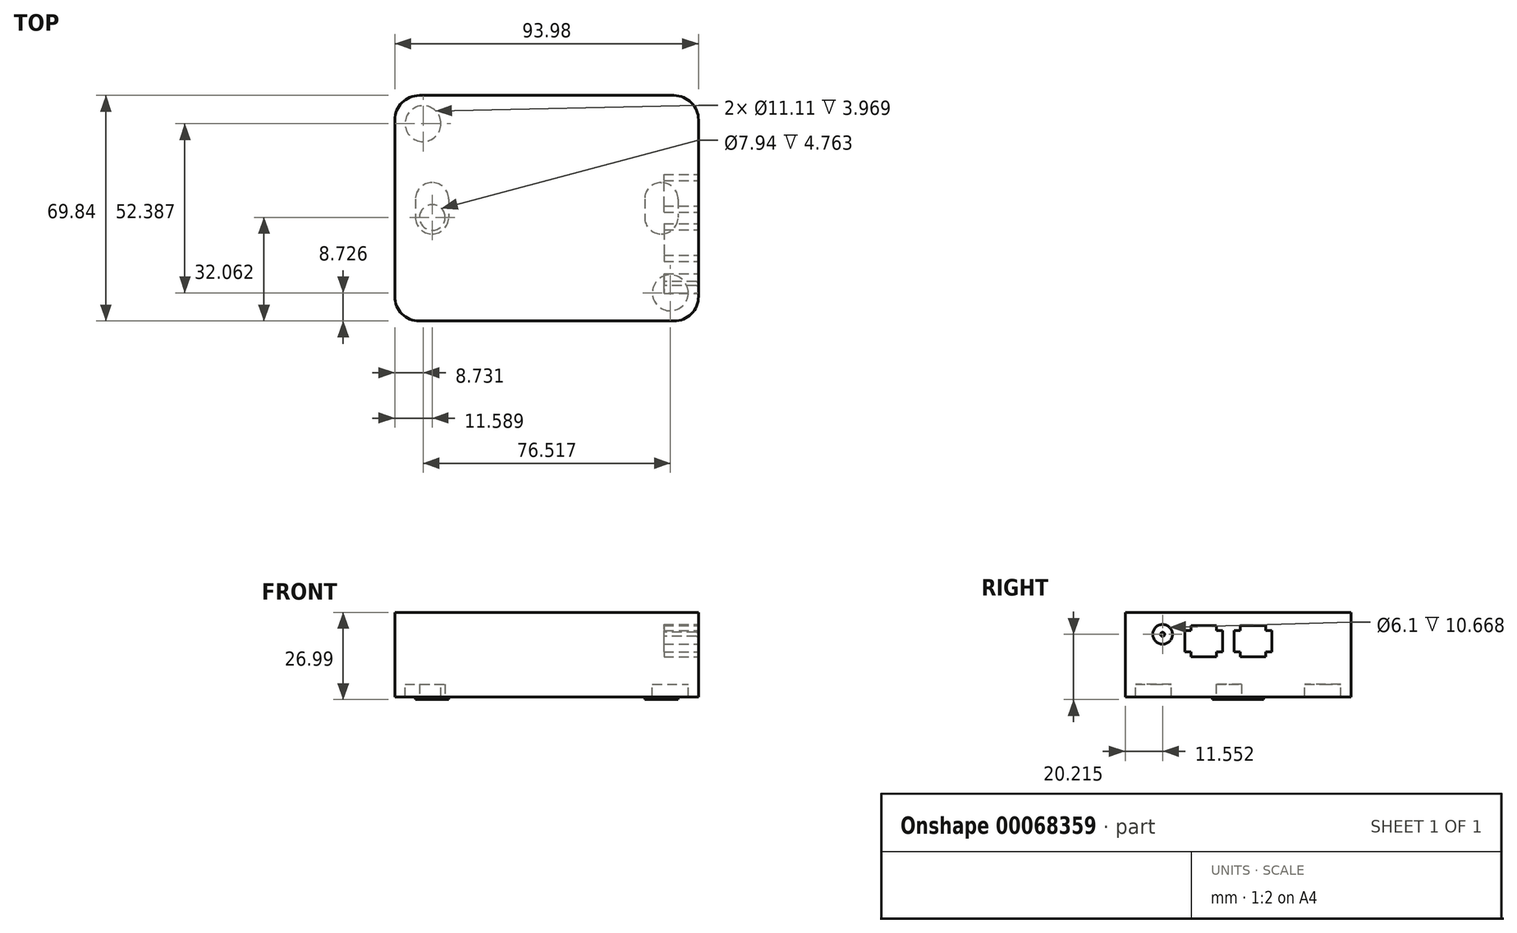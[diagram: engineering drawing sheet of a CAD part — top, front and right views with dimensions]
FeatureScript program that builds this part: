
annotation { "Feature Type Name" : "Feature", "Feature Type Description" : "" }
export const myFeature = defineFeature(function(context is Context, id is Id, definition is map)
    precondition{}
    {
        {
            var Q0;
            Q0=qCreatedBy(makeId("Top.planeOp"),FACE);
            var sketch = newSketch(context, id + "F0", { "sketchPlane" : qUnion([Q0])});
            skLineSegment(sketch, "E0.rect.bottom", {"start": v(47, -34.93) * mm, "end": v(-47, -34.93) * mm});
            skLineSegment(sketch, "E0.rect.top", {"start": v(47, 34.93) * mm, "end": v(-47, 34.92) * mm});
            skLineSegment(sketch, "E0.rect.left", {"start": v(47, -34.93) * mm, "end": v(47, 34.93) * mm});
            skLineSegment(sketch, "E0.rect.right", {"start": v(-47, -34.93) * mm, "end": v(-47, 34.92) * mm});
            skPoint(sketch, "E0.rect.middle", {"position": v(0, 0) * mm});
            skSolve(sketch);
        }
        {
            var Q0;
            Q0 = qSketchRegion(id + "F0", true);
            extrude(context, id + "F1", {"entities" : qUnion([Q0]), "depth" : 22.22 * mm});
        }
        {
            var Q0;
            Q0=makeQuery(id+"F1.opExtrude","CAP_FACE",FACE,{"disambiguationData":[OSD([sQuery(id+"F0.wireOp",EDGE,"E0.rect.bottom"),sQuery(id+"F0.wireOp",EDGE,"E0.rect.top"),sQuery(id+"F0.wireOp",EDGE,"E0.rect.left"),sQuery(id+"F0.wireOp",EDGE,"E0.rect.right")])],"isStart":true});
            var sketch = newSketch(context, id + "F2", { "sketchPlane" : qUnion([Q0])});
            skLineSegment(sketch, "E1.rect.bottom", {"start": v(30.32, -7.94) * mm, "end": v(40.64, -7.94) * mm});
            skLineSegment(sketch, "E1.rect.top", {"start": v(30.32, 7.94) * mm, "end": v(40.64, 7.94) * mm});
            skLineSegment(sketch, "E1.rect.left", {"start": v(30.32, -7.94) * mm, "end": v(30.32, 7.94) * mm});
            skLineSegment(sketch, "E1.rect.right", {"start": v(40.64, -7.94) * mm, "end": v(40.64, 7.94) * mm});
            skPoint(sketch, "E1.rect.middle", {"position": v(35.48, 0) * mm});
            skPoint(sketch, "E1.rect.middle.positionSnap0", {"position": v(47, 0) * mm});
            skPoint(sketch, "E1.rect.centerSnap0", {"position": v(47, 0) * mm});
            skLineSegment(sketch, "E2.0.0", {"start": v(47, 34.93) * mm, "end": v(-47, 34.93) * mm});
            skLineSegment(sketch, "E2.0.1", {"start": v(-47, 34.93) * mm, "end": v(-47, -34.92) * mm});
            skLineSegment(sketch, "E2.0.2", {"start": v(-47, -34.92) * mm, "end": v(47, -34.93) * mm});
            skLineSegment(sketch, "E2.0.3", {"start": v(47, -34.93) * mm, "end": v(47, 34.93) * mm});
            skLineSegment(sketch, "E3.MirrorCS", {"start": v(-30.32, 7.94) * mm, "end": v(-40.64, 7.94) * mm});
            skLineSegment(sketch, "E4.MirrorCS", {"start": v(-30.32, -7.94) * mm, "end": v(-30.32, 7.94) * mm});
            skLineSegment(sketch, "E5.MirrorCS", {"start": v(-30.32, -7.94) * mm, "end": v(-40.64, -7.94) * mm});
            skLineSegment(sketch, "E6.MirrorCS", {"start": v(-40.64, -7.94) * mm, "end": v(-40.64, 7.94) * mm});
            skSolve(sketch);
        }
        {
            var Q0;
            Q0=makeQuery(id+"F2.imprint","IMPRINT",FACE,{"disambiguationData":[TD([[makeQuery(id+"F2.imprint","IMPRINT",EDGE,{"derivedFrom":sQuery(id+"F2.wireOp",EDGE,"E3.MirrorCS")}),1.0]])]});
            var Q1;
            Q1=makeQuery(id+"F2.imprint","IMPRINT",FACE,{"disambiguationData":[TD([[makeQuery(id+"F2.imprint","IMPRINT",EDGE,{"derivedFrom":sQuery(id+"F2.wireOp",EDGE,"E1.rect.bottom")}),1.0]])]});
            extrude(context, id + "F3", {"entities" : qUnion([Q0, Q1]), "operationType" : NewBodyOperationType.ADD, "depth" : 4.76 * mm});
        }
        {
            var Q0;
            Q0=makeQuery(id+"F3.opExtrude","SWEPT_EDGE",EDGE,{"disambiguationData":[OSD([sQuery(id+"F2.wireOp",EDGE,"E3.MirrorCS"),sQuery(id+"F2.wireOp",EDGE,"E4.MirrorCS")])]});
            var Q1;
            Q1=makeQuery(id+"F3.opExtrude","SWEPT_EDGE",EDGE,{"disambiguationData":[OSD([sQuery(id+"F2.wireOp",EDGE,"E3.MirrorCS"),sQuery(id+"F2.wireOp",EDGE,"E6.MirrorCS")])]});
            var Q2;
            Q2=makeQuery(id+"F3.opExtrude","SWEPT_EDGE",EDGE,{"disambiguationData":[OSD([sQuery(id+"F2.wireOp",EDGE,"E1.rect.top"),sQuery(id+"F2.wireOp",EDGE,"E1.rect.left")])]});
            var Q3;
            Q3=makeQuery(id+"F3.opExtrude","SWEPT_EDGE",EDGE,{"disambiguationData":[OSD([sQuery(id+"F2.wireOp",EDGE,"E1.rect.top"),sQuery(id+"F2.wireOp",EDGE,"E1.rect.right")])]});
            var Q4;
            Q4=makeQuery(id+"F3.opExtrude","SWEPT_EDGE",EDGE,{"disambiguationData":[OSD([sQuery(id+"F2.wireOp",EDGE,"E1.rect.bottom"),sQuery(id+"F2.wireOp",EDGE,"E1.rect.right")])]});
            var Q5;
            Q5=makeQuery(id+"F3.opExtrude","SWEPT_EDGE",EDGE,{"disambiguationData":[OSD([sQuery(id+"F2.wireOp",EDGE,"E1.rect.bottom"),sQuery(id+"F2.wireOp",EDGE,"E1.rect.left")])]});
            var Q6;
            Q6=makeQuery(id+"F3.opExtrude","SWEPT_EDGE",EDGE,{"disambiguationData":[OSD([sQuery(id+"F2.wireOp",EDGE,"E4.MirrorCS"),sQuery(id+"F2.wireOp",EDGE,"E5.MirrorCS")])]});
            var Q7;
            Q7=makeQuery(id+"F3.opExtrude","SWEPT_EDGE",EDGE,{"disambiguationData":[OSD([sQuery(id+"F2.wireOp",EDGE,"E5.MirrorCS"),sQuery(id+"F2.wireOp",EDGE,"E6.MirrorCS")])]});
            fillet(context, id + "F4", {"entities" : qUnion([Q0, Q1, Q2, Q3, Q4, Q5, Q6, Q7]), "radius" : 5.08 * mm, "tangentPropagation" : true, "allowEdgeOverflow" : false});
        }
        {
            var Q0;
            Q0=makeQuery(id+"F1.opExtrude","CAP_FACE",FACE,{"disambiguationData":[OSD([sQuery(id+"F0.wireOp",EDGE,"E0.rect.bottom"),sQuery(id+"F0.wireOp",EDGE,"E0.rect.top"),sQuery(id+"F0.wireOp",EDGE,"E0.rect.left"),sQuery(id+"F0.wireOp",EDGE,"E0.rect.right")])],"isStart":true});
            var sketch = newSketch(context, id + "F5", { "sketchPlane" : qUnion([Q0])});
            skCircle(sketch, "E7", {"center": v(-38.26, 26.2) * mm, "radius": 5.56 * mm});
            skCircle(sketch, "E8.MirrorC", {"center": v(38.26, 26.2) * mm, "radius": 5.56 * mm});
            skCircle(sketch, "E9.MirrorC", {"center": v(-38.26, -26.2) * mm, "radius": 5.56 * mm});
            skCircle(sketch, "E10.MirrorC", {"center": v(38.26, -26.2) * mm, "radius": 5.56 * mm});
            skSolve(sketch);
        }
        {
            var Q0;
            Q0=makeQuery(id+"F5.imprint","IMPRINT",FACE,{"disambiguationData":[TD([[makeQuery(id+"F5.imprint","IMPRINT",EDGE,{"derivedFrom":sQuery(id+"F5.wireOp",EDGE,"E8.MirrorC")}),-1.0]])]});
            var Q1;
            Q1=makeQuery(id+"F5.imprint","IMPRINT",FACE,{"disambiguationData":[TD([[makeQuery(id+"F5.imprint","IMPRINT",EDGE,{"derivedFrom":sQuery(id+"F5.wireOp",EDGE,"E9.MirrorC")}),-1.0]])]});
            var Q2;
            Q2=makeQuery(id+"F5.imprint","IMPRINT",FACE,{"disambiguationData":[TD([[makeQuery(id+"F5.imprint","IMPRINT",EDGE,{"derivedFrom":sQuery(id+"F5.wireOp",EDGE,"E10.MirrorC")}),1.0]])]});
            var Q3;
            Q3=makeQuery(id+"F5.imprint","IMPRINT",FACE,{"disambiguationData":[TD([[makeQuery(id+"F5.imprint","IMPRINT",EDGE,{"derivedFrom":sQuery(id+"F5.wireOp",EDGE,"E7")}),1.0]])]});
            extrude(context, id + "F6", {"entities" : qUnion([Q0, Q1, Q2, Q3]), "operationType" : NewBodyOperationType.ADD, "depth" : 3.97 * mm});
        }
        {
            var Q0;
            Q0=makeQuery(id+"F3.opExtrude","CAP_FACE",FACE,{"disambiguationData":[OSD([sQuery(id+"F2.wireOp",EDGE,"E3.MirrorCS"),sQuery(id+"F2.wireOp",EDGE,"E4.MirrorCS"),sQuery(id+"F2.wireOp",EDGE,"E5.MirrorCS"),sQuery(id+"F2.wireOp",EDGE,"E6.MirrorCS")])],"isStart":false});
            var sketch = newSketch(context, id + "F7", { "sketchPlane" : qUnion([Q0])});
            skCircle(sketch, "E11", {"center": v(-35.4, 2.86) * mm, "radius": 3.97 * mm});
            skCircle(sketch, "E12.MirrorC", {"center": v(35.4, 2.86) * mm, "radius": 3.97 * mm});
            skSolve(sketch);
        }
        {
            var Q0;
            Q0=makeQuery(id+"F1.opExtrude","SWEPT_EDGE",EDGE,{"disambiguationData":[OSD([sQuery(id+"F0.wireOp",EDGE,"E0.rect.bottom"),sQuery(id+"F0.wireOp",EDGE,"E0.rect.right")])]});
            var Q1;
            Q1=makeQuery(id+"F1.opExtrude","SWEPT_EDGE",EDGE,{"disambiguationData":[OSD([sQuery(id+"F0.wireOp",EDGE,"E0.rect.bottom"),sQuery(id+"F0.wireOp",EDGE,"E0.rect.left")])]});
            var Q2;
            Q2=makeQuery(id+"F1.opExtrude","SWEPT_EDGE",EDGE,{"disambiguationData":[OSD([sQuery(id+"F0.wireOp",EDGE,"E0.rect.top"),sQuery(id+"F0.wireOp",EDGE,"E0.rect.left")])]});
            var Q3;
            Q3=makeQuery(id+"F1.opExtrude","SWEPT_EDGE",EDGE,{"disambiguationData":[OSD([sQuery(id+"F0.wireOp",EDGE,"E0.rect.top"),sQuery(id+"F0.wireOp",EDGE,"E0.rect.right")])]});
            fillet(context, id + "F8", {"entities" : qUnion([Q0, Q1, Q2, Q3]), "radius" : 7.62 * mm, "tangentPropagation" : true, "allowEdgeOverflow" : false});
        }
        {
            var Q0;
            Q0=makeQuery(id+"F1.opExtrude","SWEPT_FACE",FACE,{"disambiguationData":[OSD([sQuery(id+"F0.wireOp",EDGE,"E0.rect.left")])]});
            var sketch = newSketch(context, id + "F9", { "sketchPlane" : qUnion([Q0])});
            skLineSegment(sketch, "E13.rect.bottom", {"start": v(-18.92, 8.26) * mm, "end": v(-27.81, 8.26) * mm});
            skLineSegment(sketch, "E13.rect.top", {"start": v(-18.92, 18.92) * mm, "end": v(-27.81, 18.92) * mm});
            skLineSegment(sketch, "E13.rect.left", {"start": v(-18.92, 8.26) * mm, "end": v(-18.92, 18.92) * mm});
            skLineSegment(sketch, "E13.rect.right", {"start": v(-27.81, 8.26) * mm, "end": v(-27.81, 18.92) * mm});
            skPoint(sketch, "E13.rect.middle", {"position": v(-23.37, 13.59) * mm});
            skCircle(sketch, "E14", {"center": v(-23.37, 15.46) * mm, "radius": 3.05 * mm});
            skLineSegment(sketch, "E15.rect.bottom", {"start": v(-3.02, 7.62) * mm, "end": v(-18.26, 7.62) * mm});
            skLineSegment(sketch, "E15.rect.top", {"start": v(-3.02, 19.05) * mm, "end": v(-18.26, 19.05) * mm});
            skLineSegment(sketch, "E15.rect.left", {"start": v(-3.02, 7.62) * mm, "end": v(-3.02, 19.05) * mm});
            skLineSegment(sketch, "E15.rect.right", {"start": v(-18.26, 7.62) * mm, "end": v(-18.26, 19.05) * mm});
            skPoint(sketch, "E15.rect.middle", {"position": v(-10.64, 13.33) * mm});
            skLineSegment(sketch, "E16.rect.bottom", {"start": v(-4.8, 10.03) * mm, "end": v(-16.49, 10.03) * mm});
            skLineSegment(sketch, "E16.rect.top", {"start": v(-4.8, 16.64) * mm, "end": v(-16.49, 16.64) * mm});
            skLineSegment(sketch, "E16.rect.left", {"start": v(-4.8, 10.03) * mm, "end": v(-4.8, 16.64) * mm});
            skLineSegment(sketch, "E16.rect.right", {"start": v(-16.49, 10.03) * mm, "end": v(-16.49, 16.64) * mm});
            skLineSegment(sketch, "E17.rect.bottom", {"start": v(-6.7, 18.16) * mm, "end": v(-14.58, 18.16) * mm});
            skLineSegment(sketch, "E17.rect.top", {"start": v(-6.7, 8.5) * mm, "end": v(-14.58, 8.5) * mm});
            skLineSegment(sketch, "E17.rect.left", {"start": v(-6.7, 18.16) * mm, "end": v(-6.7, 8.5) * mm});
            skLineSegment(sketch, "E17.rect.right", {"start": v(-14.58, 18.16) * mm, "end": v(-14.58, 8.5) * mm});
            skLineSegment(sketch, "E18.MirrorCS", {"start": v(-1.25, 10.03) * mm, "end": v(-1.25, 16.64) * mm});
            skLineSegment(sketch, "E19.MirrorCS", {"start": v(-1.25, 16.64) * mm, "end": v(10.44, 16.64) * mm});
            skLineSegment(sketch, "E20.MirrorCS", {"start": v(0.66, 18.16) * mm, "end": v(0.66, 8.5) * mm});
            skLineSegment(sketch, "E21.MirrorCS", {"start": v(0.66, 18.16) * mm, "end": v(8.53, 18.16) * mm});
            skLineSegment(sketch, "E22.MirrorCS", {"start": v(-3.02, 19.05) * mm, "end": v(12.22, 19.05) * mm});
            skLineSegment(sketch, "E23.MirrorCS", {"start": v(12.22, 7.62) * mm, "end": v(12.22, 19.05) * mm});
            skLineSegment(sketch, "E24.MirrorCS", {"start": v(10.44, 10.03) * mm, "end": v(10.44, 16.64) * mm});
            skLineSegment(sketch, "E25.MirrorCS", {"start": v(8.53, 18.16) * mm, "end": v(8.53, 8.5) * mm});
            skLineSegment(sketch, "E26.MirrorCS", {"start": v(0.66, 8.5) * mm, "end": v(8.53, 8.5) * mm});
            skLineSegment(sketch, "E27.MirrorCS", {"start": v(-1.25, 10.03) * mm, "end": v(10.44, 10.03) * mm});
            skLineSegment(sketch, "E28.MirrorCS", {"start": v(-3.02, 7.62) * mm, "end": v(12.22, 7.62) * mm});
            skSolve(sketch);
        }
        {
            var Q0;
            {var subQ5=sQuery(id+"F9.wireOp",EDGE,"E17.rect.bottom");Q0=makeQuery(id+"F9.imprint","IMPRINT",FACE,{"disambiguationData":[TD([[makeQuery(id+"F9.imprint","IMPRINT",EDGE,{"derivedFrom":subQ5}),1.0]])]});}
            var Q1;
            {var subQ0=sQuery(id+"F9.wireOp",EDGE,"E16.rect.left");Q1=makeQuery(id+"F9.imprint","IMPRINT",FACE,{"disambiguationData":[TD([[makeQuery(id+"F9.imprint","IMPRINT",EDGE,{"derivedFrom":subQ0}),1.0]])]});}
            var Q2;
            {var subQ0=sQuery(id+"F9.wireOp",EDGE,"E17.rect.left");var subQ1=sQuery(id+"F9.wireOp",EDGE,"E16.rect.bottom");var subQ2=makeQuery(id+"F9.imprint","INTERSECT",VERTEX,{"derivedFrom":[subQ1,subQ0]});Q2=makeQuery(id+"F9.imprint","IMPRINT",FACE,{"disambiguationData":[TD([[makeQuery(id+"F9.imprint","IMPRINT",EDGE,{"disambiguationData":[TD([[subQ2,-1.0]])],"derivedFrom":subQ1}),-1.0]])]});}
            var Q3;
            {var subQ0=sQuery(id+"F9.wireOp",EDGE,"E16.rect.right");Q3=makeQuery(id+"F9.imprint","IMPRINT",FACE,{"disambiguationData":[TD([[makeQuery(id+"F9.imprint","IMPRINT",EDGE,{"derivedFrom":subQ0}),-1.0]])]});}
            var Q4;
            {var subQ5=sQuery(id+"F9.wireOp",EDGE,"E17.rect.top");Q4=makeQuery(id+"F9.imprint","IMPRINT",FACE,{"disambiguationData":[TD([[makeQuery(id+"F9.imprint","IMPRINT",EDGE,{"derivedFrom":subQ5}),-1.0]])]});}
            extrude(context, id + "F10", {"entities" : qUnion([Q0, Q1, Q2, Q3, Q4]), "operationType" : NewBodyOperationType.REMOVE, "oppositeDirection" : true, "depth" : 10.67 * mm});
        }
        {
            var Q0;
            {var subQ0=sQuery(id+"F9.wireOp",EDGE,"E18.MirrorCS");Q0=makeQuery(id+"F9.imprint","IMPRINT",FACE,{"disambiguationData":[TD([[makeQuery(id+"F9.imprint","IMPRINT",EDGE,{"derivedFrom":subQ0}),-1.0]])]});}
            var Q1;
            {var subQ5=sQuery(id+"F9.wireOp",EDGE,"E21.MirrorCS");Q1=makeQuery(id+"F9.imprint","IMPRINT",FACE,{"disambiguationData":[TD([[makeQuery(id+"F9.imprint","IMPRINT",EDGE,{"derivedFrom":subQ5}),-1.0]])]});}
            var Q2;
            {var subQ0=sQuery(id+"F9.wireOp",EDGE,"E26.MirrorCS");Q2=makeQuery(id+"F9.imprint","IMPRINT",FACE,{"disambiguationData":[TD([[makeQuery(id+"F9.imprint","IMPRINT",EDGE,{"derivedFrom":subQ0}),1.0]])]});}
            var Q3;
            {var subQ0=sQuery(id+"F9.wireOp",EDGE,"E20.MirrorCS");var subQ1=sQuery(id+"F9.wireOp",EDGE,"E19.MirrorCS");var subQ2=makeQuery(id+"F9.imprint","INTERSECT",VERTEX,{"derivedFrom":[subQ1,subQ0]});Q3=makeQuery(id+"F9.imprint","IMPRINT",FACE,{"disambiguationData":[TD([[makeQuery(id+"F9.imprint","IMPRINT",EDGE,{"disambiguationData":[TD([[subQ2,-1.0]])],"derivedFrom":subQ1}),-1.0]])]});}
            var Q4;
            {var subQ0=sQuery(id+"F9.wireOp",EDGE,"E24.MirrorCS");Q4=makeQuery(id+"F9.imprint","IMPRINT",FACE,{"disambiguationData":[TD([[makeQuery(id+"F9.imprint","IMPRINT",EDGE,{"derivedFrom":subQ0}),1.0]])]});}
            extrude(context, id + "F11", {"entities" : qUnion([Q0, Q1, Q2, Q3, Q4]), "operationType" : NewBodyOperationType.REMOVE, "oppositeDirection" : true, "depth" : 10.67 * mm});
        }
        {
            var Q0;
            {var subQ0=sQuery(id+"F9.wireOp",EDGE,"E14");var subQ1=sQuery(id+"F0.wireOp",EDGE,"E0.rect.left");var subQ2=makeQuery(id+"F8.opFillet","BLEND_EDGE",EDGE,{"blendedFrom":[makeQuery(id+"F1.opExtrude","SWEPT_EDGE",EDGE,{"disambiguationData":[OSD([sQuery(id+"F0.wireOp",EDGE,"E0.rect.bottom"),subQ1])]}),makeQuery(id+"F1.opExtrude","SWEPT_FACE",FACE,{"disambiguationData":[OSD([subQ1])]})],"blendedInto":[makeQuery(id+"F1.opExtrude","SWEPT_FACE",FACE,{"disambiguationData":[OSD([subQ1])]})]});var subQ3=makeQuery(id+"F9.imprint","INTERSECT",VERTEX,{"disambiguationData":[OD(0.0)],"derivedFrom":[subQ2,subQ0]});Q0=makeQuery(id+"F9.imprint","IMPRINT",FACE,{"disambiguationData":[TD([[makeQuery(id+"F9.imprint","IMPRINT",EDGE,{"disambiguationData":[TD([[subQ3,-1.0]])],"derivedFrom":subQ0}),1.0]])]});}
            var Q1;
            {var subQ0=sQuery(id+"F9.wireOp",EDGE,"E14");var subQ1=sQuery(id+"F0.wireOp",EDGE,"E0.rect.left");var subQ2=makeQuery(id+"F8.opFillet","BLEND_EDGE",EDGE,{"blendedFrom":[makeQuery(id+"F1.opExtrude","SWEPT_EDGE",EDGE,{"disambiguationData":[OSD([sQuery(id+"F0.wireOp",EDGE,"E0.rect.bottom"),subQ1])]}),makeQuery(id+"F1.opExtrude","SWEPT_FACE",FACE,{"disambiguationData":[OSD([subQ1])]})],"blendedInto":[makeQuery(id+"F1.opExtrude","SWEPT_FACE",FACE,{"disambiguationData":[OSD([subQ1])]})]});var subQ3=makeQuery(id+"F9.imprint","INTERSECT",VERTEX,{"disambiguationData":[OD(0.0)],"derivedFrom":[subQ2,subQ0]});Q1=makeQuery(id+"F9.imprint","IMPRINT",FACE,{"disambiguationData":[TD([[makeQuery(id+"F9.imprint","IMPRINT",EDGE,{"disambiguationData":[TD([[subQ3,1.0]])],"derivedFrom":subQ0}),1.0]])]});}
            extrude(context, id + "F12", {"entities" : qUnion([Q0, Q1]), "operationType" : NewBodyOperationType.REMOVE, "oppositeDirection" : true, "depth" : 10.67 * mm});
        }
        {
            var Q0;
            Q0=makeQuery(id+"F12.boolean.opBoolean","COPY",FACE,{"derivedFrom":makeQuery(id+"F12.opExtrude","CAP_FACE",FACE,{"disambiguationData":[OSD([sQuery(id+"F9.wireOp",EDGE,"E14")])],"isStart":false})});
            var sketch = newSketch(context, id + "F13", { "sketchPlane" : qUnion([Q0])});
            skCircle(sketch, "E29", {"center": v(-23.37, 15.46) * mm, "radius": 0.64 * mm});
            skSolve(sketch);
        }
        {
            var Q0;
            Q0 = qSketchRegion(id + "F13", true);
            extrude(context, id + "F14", {"entities" : qUnion([Q0]), "operationType" : NewBodyOperationType.ADD, "depth" : 10.67 * mm});
        }
        {
            var Q0;
            Q0=makeQuery(id+"F14.opExtrude","CAP_EDGE",EDGE,{"disambiguationData":[OSD([sQuery(id+"F13.wireOp",EDGE,"E29")])],"isStart":false});
            fillet(context, id + "F15", {"entities" : qUnion([Q0]), "radius" : 0.6 * mm, "allowEdgeOverflow" : false});
        }
        {
            var Q0;
            Q0=makeQuery(id+"F7.imprint","IMPRINT",FACE,{"disambiguationData":[TD([[makeQuery(id+"F7.imprint","IMPRINT",EDGE,{"derivedFrom":sQuery(id+"F7.wireOp",EDGE,"E11")}),1.0]])]});
            var Q1;
            Q1=makeQuery(id+"F7.imprint","IMPRINT",FACE,{"disambiguationData":[TD([[makeQuery(id+"F7.imprint","IMPRINT",EDGE,{"derivedFrom":sQuery(id+"F7.wireOp",EDGE,"E12.MirrorC")}),-1.0]])]});
            extrude(context, id + "F16", {"entities" : qUnion([Q0, Q1]), "operationType" : NewBodyOperationType.REMOVE, "oppositeDirection" : true, "depth" : 4.76 * mm});
        }
    });
